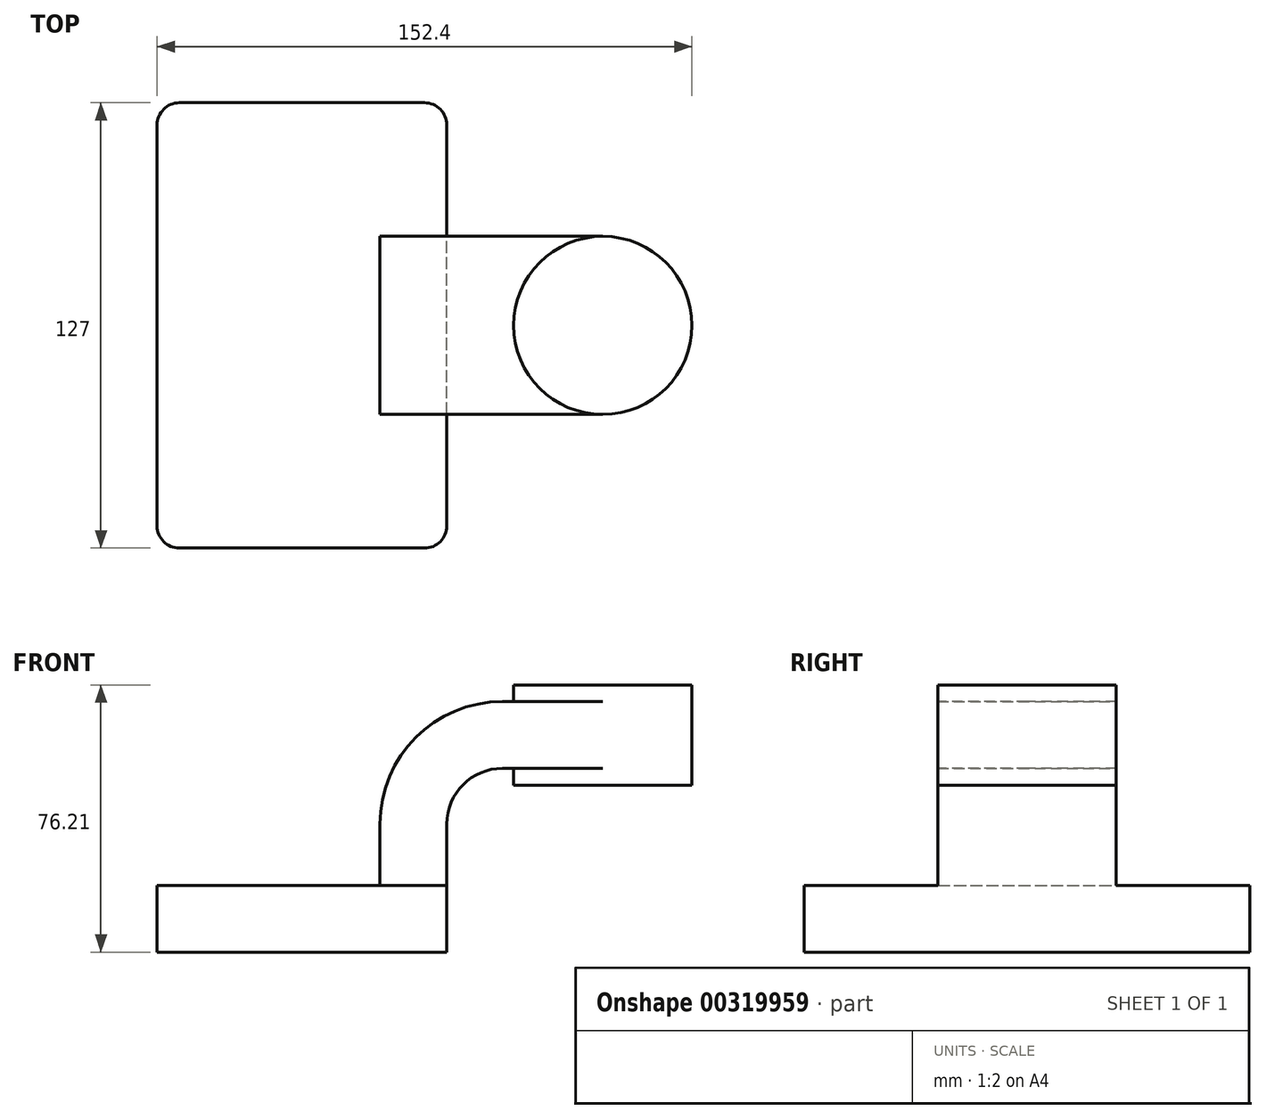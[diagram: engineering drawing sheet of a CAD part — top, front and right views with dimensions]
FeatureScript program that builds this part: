
annotation { "Feature Type Name" : "Feature", "Feature Type Description" : "" }
export const myFeature = defineFeature(function(context is Context, id is Id, definition is map)
    precondition{}
    {
        {
            var Q0;
            Q0=qCreatedBy(makeId("Front.planeOp"),FACE);
            var sketch = newSketch(context, id + "F0", { "sketchPlane" : qUnion([Q0])});
            skLineSegment(sketch, "E0.bottom", {"start": v(-41.27, 9.53) * mm, "end": v(41.27, 9.53) * mm});
            skLineSegment(sketch, "E0.top", {"start": v(-41.27, -9.52) * mm, "end": v(41.28, -9.52) * mm});
            skLineSegment(sketch, "E0.left", {"start": v(-41.28, 9.53) * mm, "end": v(-41.27, -9.52) * mm});
            skLineSegment(sketch, "E0.right", {"start": v(41.28, 9.53) * mm, "end": v(41.28, -9.52) * mm});
            skPoint(sketch, "E0.middle", {"position": v(0, 0) * mm});
            skLineSegment(sketch, "E1.bottom", {"start": v(111.12, 66.68) * mm, "end": v(60.32, 66.68) * mm});
            skLineSegment(sketch, "E1.top", {"start": v(111.12, 38.1) * mm, "end": v(60.32, 38.1) * mm});
            skLineSegment(sketch, "E1.left", {"start": v(111.12, 66.68) * mm, "end": v(111.12, 38.1) * mm});
            skLineSegment(sketch, "E1.right", {"start": v(60.32, 66.68) * mm, "end": v(60.32, 38.1) * mm});
            skPoint(sketch, "E1.middle", {"position": v(85.72, 52.39) * mm});
            skLineSegment(sketch, "E2", {"start": v(41.27, 9.53) * mm, "end": v(41.27, 27) * mm});
            skArc(sketch, "E3", {"start": v(41.27, 27) * mm, "mid": v(45.92, 38.23) * mm, "end": v(57.15, 42.88) * mm});
            skLineSegment(sketch, "E4", {"start": v(57.15, 42.88) * mm, "end": v(85.72, 42.88) * mm});
            skLineSegment(sketch, "E5.0", {"start": v(57.15, 61.93) * mm, "end": v(85.72, 61.93) * mm});
            skArc(sketch, "E5.1", {"start": v(22.22, 27) * mm, "mid": v(32.45, 51.7) * mm, "end": v(57.15, 61.93) * mm});
            skLineSegment(sketch, "E5.2", {"start": v(22.22, 9.53) * mm, "end": v(22.22, 27) * mm});
            skLineSegment(sketch, "E6", {"start": v(85.72, 42.88) * mm, "end": v(85.72, 66.68) * mm});
            skFitSpline(sketch, "E7", {"points": [v(-41.28, 9.52) * mm, v(57.15, 61.93) * mm], "startDerivative": vector(6.62, 90.2) * mm, "endDerivative": vector(124.33, -2.99) * mm});
            skLineSegment(sketch, "E8", {"start": v(85.73, 42.88) * mm, "end": v(85.73, 38.1) * mm});
            skLineSegment(sketch, "E9", {"start": v(85.72, 38.1) * mm, "end": v(85.72, 42.88) * mm});
            skSolve(sketch);
        }
        {
            var Q0;
            Q0=makeQuery(id+"F0.imprint","IMPRINT",FACE,{"disambiguationData":[TD([[makeQuery(id+"F0.imprint","IMPRINT",EDGE,{"derivedFrom":sQuery(id+"F0.wireOp",EDGE,"E0.top")}),1.0]])]});
            extrude(context, id + "F1", {"entities" : qUnion([Q0]), "endBound" : BoundingType.SYMMETRIC, "depth" : 127 * mm});
        }
        {
            var Q0;
            {var subQ1=sQuery(id+"F0.wireOp",EDGE,"E2");Q0=makeQuery(id+"F0.imprint","IMPRINT",FACE,{"disambiguationData":[TD([[makeQuery(id+"F0.imprint","IMPRINT",EDGE,{"derivedFrom":subQ1}),1.0]])]});}
            var Q1;
            {var subQ0=sQuery(id+"F0.wireOp",EDGE,"E5.0");var subQ1=sQuery(id+"F0.wireOp",EDGE,"E1.right");var subQ2=makeQuery(id+"F0.imprint","INTERSECT",VERTEX,{"derivedFrom":[subQ1,subQ0]});Q1=makeQuery(id+"F0.imprint","IMPRINT",FACE,{"disambiguationData":[TD([[makeQuery(id+"F0.imprint","IMPRINT",EDGE,{"disambiguationData":[TD([[subQ2,-1.0]])],"derivedFrom":subQ1}),1.0]])]});}
            extrude(context, id + "F2", {"entities" : qUnion([Q0, Q1]), "operationType" : NewBodyOperationType.ADD, "endBound" : BoundingType.SYMMETRIC, "depth" : 50.8 * mm});
        }
        {
            var Q0;
            Q0=makeQuery(id+"F0.imprint","IMPRINT",FACE,{"disambiguationData":[TD([[makeQuery(id+"F0.imprint","IMPRINT",EDGE,{"derivedFrom":sQuery(id+"F0.wireOp",EDGE,"E5.1")}),1.0]])]});
            extrude(context, id + "F3", {"entities" : qUnion([Q0]), "operationType" : NewBodyOperationType.ADD, "endBound" : BoundingType.SYMMETRIC, "depth" : 15.88 * mm});
        }
        {
            var Q0;
            {var subQ3=sQuery(id+"F0.wireOp",EDGE,"E1.left");Q0=makeQuery(id+"F0.imprint","IMPRINT",FACE,{"disambiguationData":[TD([[makeQuery(id+"F0.imprint","IMPRINT",EDGE,{"derivedFrom":subQ3}),-1.0]])]});}
            var Q1;
            Q1=sQuery(id+"F0.wireOp",EDGE,"E6");
            revolve(context, id + "F4", {"operationType" : NewBodyOperationType.ADD, "entities" : qUnion([Q0]), "axis" : qUnion([Q1]), "revolveType" : RevolveType.FULL});
        }
        {
            var Q0;
            Q0=makeQuery(id+"F1.opExtrude","CAP_EDGE",EDGE,{"disambiguationData":[OSD([sQuery(id+"F0.wireOp",EDGE,"E0.left")])],"isStart":false});
            var Q1;
            Q1=makeQuery(id+"F1.opExtrude","CAP_EDGE",EDGE,{"disambiguationData":[OSD([sQuery(id+"F0.wireOp",EDGE,"E0.right")])],"isStart":false});
            var Q2;
            Q2=makeQuery(id+"F1.opExtrude","CAP_EDGE",EDGE,{"disambiguationData":[OSD([sQuery(id+"F0.wireOp",EDGE,"E0.right")])],"isStart":true});
            var Q3;
            Q3=makeQuery(id+"F1.opExtrude","CAP_EDGE",EDGE,{"disambiguationData":[OSD([sQuery(id+"F0.wireOp",EDGE,"E0.left")])],"isStart":true});
            fillet(context, id + "F5", {"entities" : qUnion([Q0, Q1, Q2, Q3]), "radius" : 6.35 * mm, "tangentPropagation" : true, "allowEdgeOverflow" : false});
        }
    });
